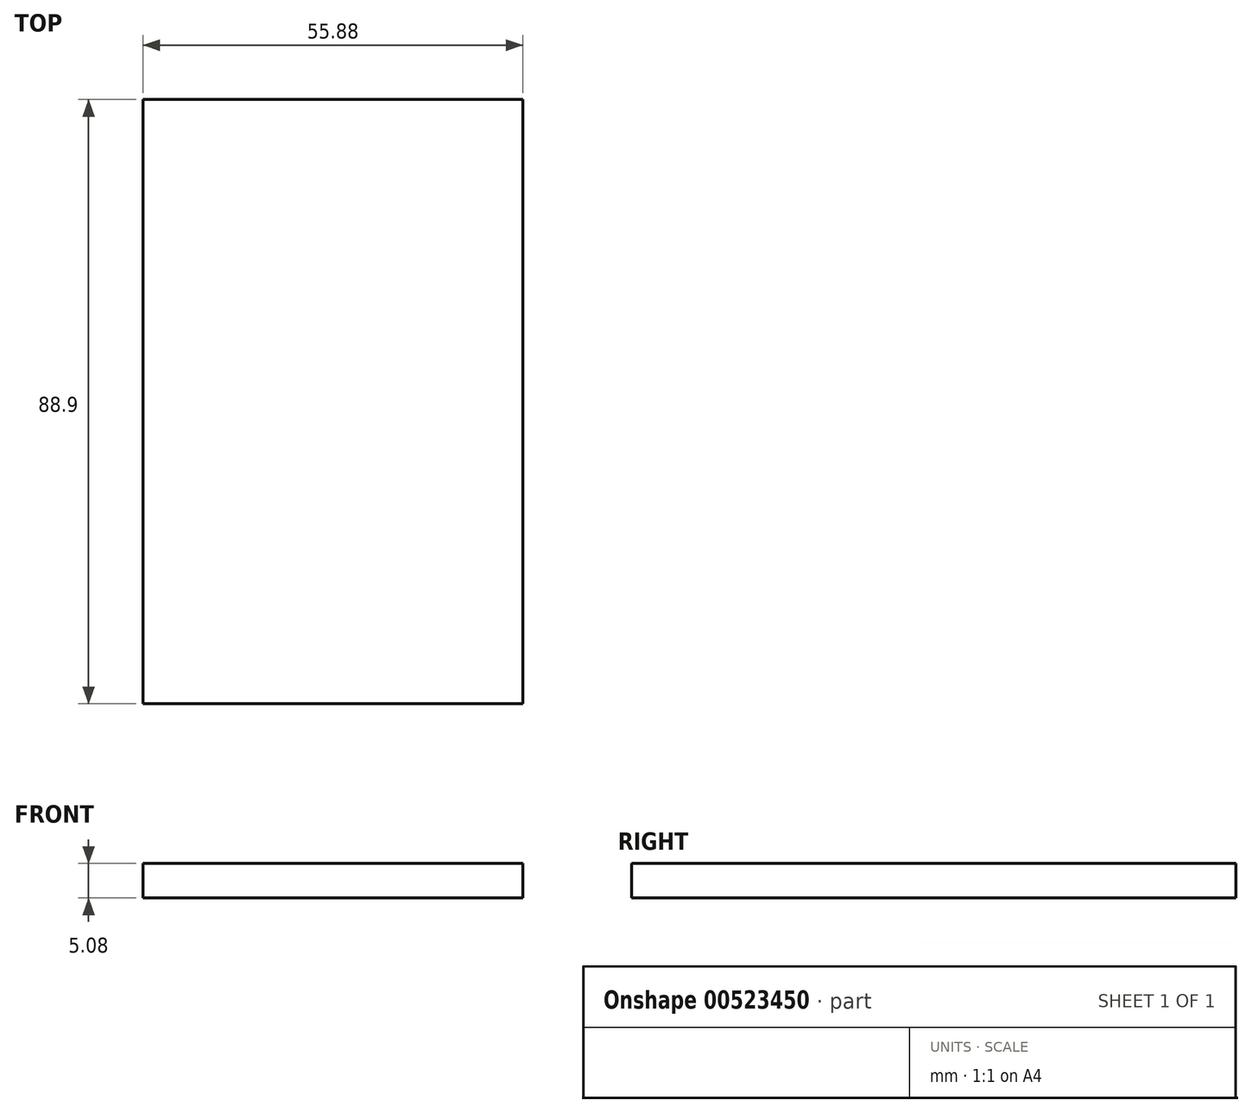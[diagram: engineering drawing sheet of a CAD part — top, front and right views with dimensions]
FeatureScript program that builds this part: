
annotation { "Feature Type Name" : "Feature", "Feature Type Description" : "" }
export const myFeature = defineFeature(function(context is Context, id is Id, definition is map)
    precondition{}
    {
        {
            var Q0;
            Q0=qCreatedBy(makeId("Top.planeOp"),FACE);
            var sketch = newSketch(context, id + "F0", { "sketchPlane" : qUnion([Q0])});
            skLineSegment(sketch, "E0.bottom", {"start": v(-24.63, 55.91) * mm, "end": v(31.25, 55.91) * mm});
            skLineSegment(sketch, "E0.top", {"start": v(-24.63, -32.99) * mm, "end": v(31.25, -32.99) * mm});
            skLineSegment(sketch, "E0.left", {"start": v(-24.63, 55.91) * mm, "end": v(-24.63, -32.99) * mm});
            skLineSegment(sketch, "E0.right", {"start": v(31.25, 55.91) * mm, "end": v(31.25, -32.99) * mm});
            skSolve(sketch);
        }
        {
            var Q0;
            Q0=makeQuery(id+"F0.imprint","IMPRINT",FACE,{"disambiguationData":[TD([[makeQuery(id+"F0.imprint","IMPRINT",EDGE,{"derivedFrom":sQuery(id+"F0.wireOp",EDGE,"E0.bottom")}),-1.0]])]});
            extrude(context, id + "F1", {"entities" : qUnion([Q0]), "depth" : 5.08 * mm, "offsetDistance" : 25.4 * mm});
        }
    });
